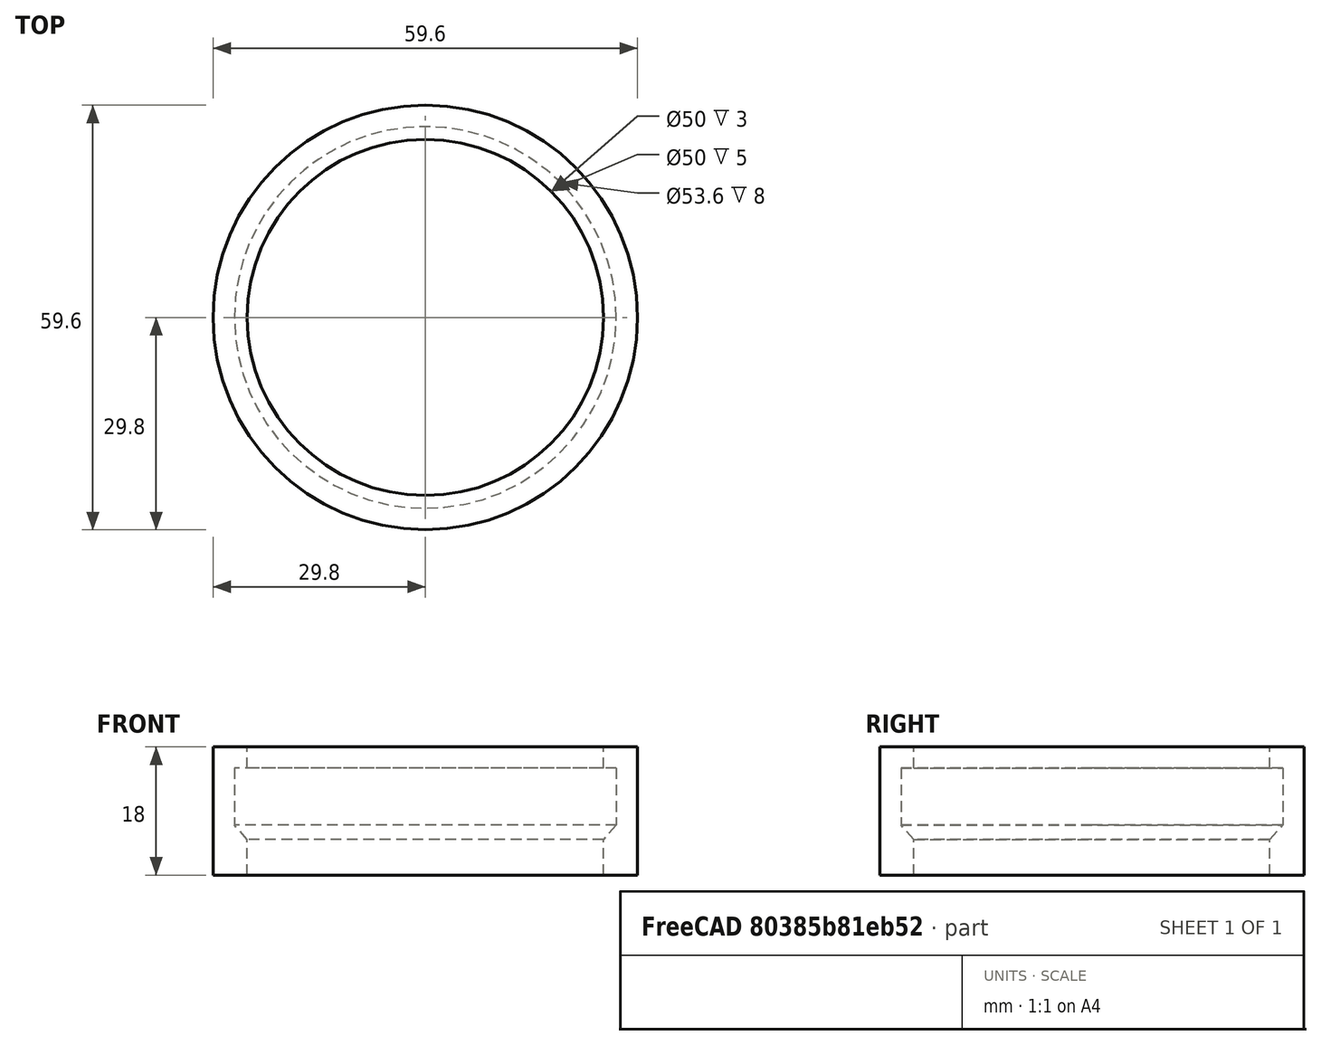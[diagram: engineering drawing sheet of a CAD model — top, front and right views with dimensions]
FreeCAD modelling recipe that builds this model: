
FCSTD DOCUMENT  (FreeCAD 1.1R39748 (Git))
Label: горло
License: All rights reserved
LicenseURL: https://en.wikipedia.org/wiki/All_rights_reserved
objects: App::Point×1, Sketcher::SketchObject×1, PartDesign::Revolution×1, PartDesign::Body×1
note: 6 computed .brp shape members not serialized (recipe doc carries the construction recipe); baked Part::Feature solids carry a one-line shape summary decoded from their .brp

FEATURE [App::Point] Origin001
  Role = Origin
FEATURE [Sketcher::SketchObject] Sketch
  ArcFitTolerance = 1e-06
  AttachmentSupport = -> [XZ_Plane]
  ExternalTypes = [0]
  FullyConstrained = true
  MakeInternals = false
  MapMode = 5
  Placement = pos=(0,0,0) rot=(1,0,0;1.5708rad)
  expr: Constraints[2] = 50 / 2
  expr: Constraints[7] = (50 + 1.8 * 2) / 2
  sketch-geometry (8):
    g0: LineSegment StartX=25 StartY=0 StartZ=0 EndX=25 EndY=5 EndZ=0
    g1: LineSegment StartX=26.8 StartY=14.8 StartZ=0 EndX=26.8 EndY=6.8 EndZ=0
    g2: LineSegment StartX=26.8 StartY=6.8 StartZ=0 EndX=25 EndY=5 EndZ=0
    g3: LineSegment StartX=26.8 StartY=14.8 StartZ=0 EndX=25 EndY=14.8 EndZ=0
    g4: LineSegment StartX=25 StartY=14.8 StartZ=0 EndX=25 EndY=17.8 EndZ=0
    g5: LineSegment StartX=25 StartY=17.8 StartZ=0 EndX=29.8 EndY=17.8 EndZ=0
    g6: LineSegment StartX=29.8 StartY=17.8 StartZ=0 EndX=29.8 EndY=0 EndZ=0
    g7: LineSegment StartX=29.8 StartY=0 StartZ=0 EndX=25 EndY=0 EndZ=0
  constraints (24):
    c: PointOnObject(g0,g-1)
    c: Vertical(g0)
    c: Distance(g0,g-1) = 25
    c: Vertical(g1)
    c: Coincident(g2,g0)
    c: Coincident(g1,g2)
    c: Distance(g1,g1) = 8
    c: DistanceX(g-1,g1) = 26.8
    c: Coincident(g3,g1)
    c: Horizontal(g3)
    c: DistanceX(g-1,g3) = 25
    c: Coincident(g4,g3)
    c: Vertical(g4)
    c: Coincident(g5,g4)
    c: Horizontal(g5)
    c: Coincident(g6,g5)
    c: PointOnObject(g6,g-1)
    c: Vertical(g6)
    c: Coincident(g7,g6)
    c: Coincident(g7,g0)
    c: Distance(g3,g4) = 3
    c: DistanceX(g1,g6) = 3
    c: DistanceY(g0,g0) = 5
    c: Angle(g0,g2) = 2.35619
FEATURE [PartDesign::Revolution] Revolution
  Angle = 360
  Angle2 = 60
  Axis = (0,2e-16,1)
  Base = (0,0,0)
  Placement = pos=(0,0,0) rot=(1,0,0;1.5708rad)
  Profile = -> Sketch
  ReferenceAxis = -> Sketch [V_Axis]
  Reversed = true
  Suppressed = false
  Type = 0
FEATURE [PartDesign::Body] Body
  AllowCompound = false
  Group = -> [Sketch,Revolution]
  Origin = -> Origin
  Tip = -> Revolution
